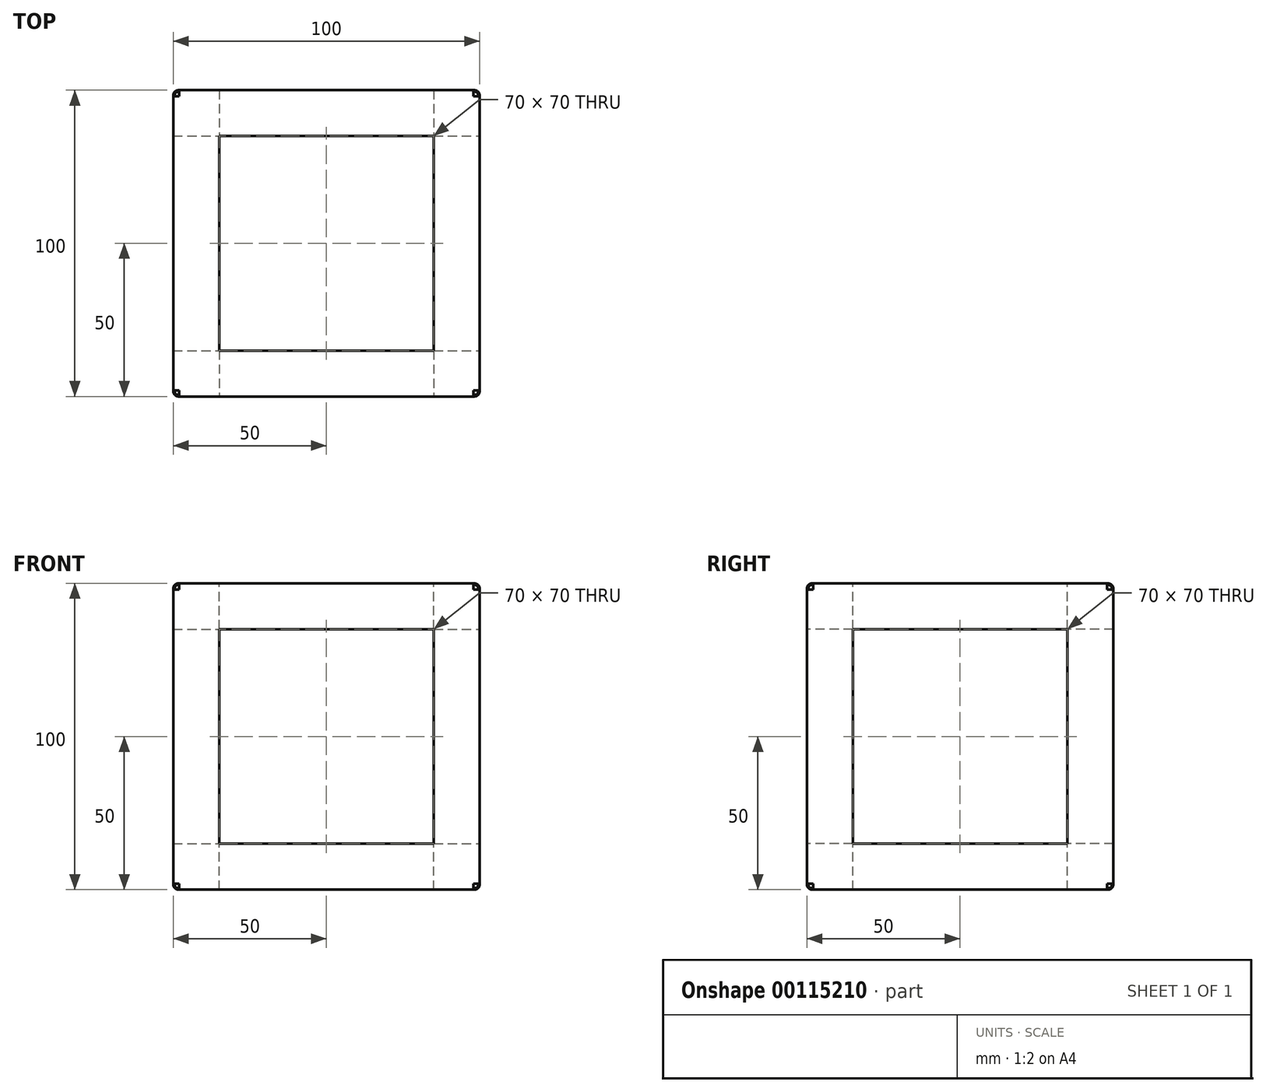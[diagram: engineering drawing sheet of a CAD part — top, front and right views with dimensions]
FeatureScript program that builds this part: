
annotation { "Feature Type Name" : "Feature", "Feature Type Description" : "" }
export const myFeature = defineFeature(function(context is Context, id is Id, definition is map)
    precondition{}
    {
        {
            var Q0;
            Q0=qCreatedBy(makeId("Front.planeOp"),FACE);
            var sketch = newSketch(context, id + "F0", { "sketchPlane" : qUnion([Q0])});
            skLineSegment(sketch, "E0.bottom", {"start": v(50, 50) * mm, "end": v(-50, 50) * mm});
            skLineSegment(sketch, "E0.top", {"start": v(50, -50) * mm, "end": v(-50, -50) * mm});
            skLineSegment(sketch, "E0.left", {"start": v(50, 50) * mm, "end": v(50, -50) * mm});
            skLineSegment(sketch, "E0.right", {"start": v(-50, 50) * mm, "end": v(-50, -50) * mm});
            skPoint(sketch, "E0.middle", {"position": v(0, 0) * mm});
            skSolve(sketch);
        }
        {
            var Q0;
            Q0 = qSketchRegion(id + "F0", true);
            var Q1;
            Q1=makeQuery(id+"F0.imprint","IMPRINT",FACE,{"disambiguationData":[TD([[makeQuery(id+"F0.imprint","IMPRINT",EDGE,{"derivedFrom":sQuery(id+"F0.wireOp",EDGE,"E0.bottom")}),1.0]])]});
            extrude(context, id + "F1", {"entities" : qUnion([Q0, Q1]), "endBound" : BoundingType.SYMMETRIC, "depth" : 100 * mm});
        }
        {
            var Q0;
            Q0=makeQuery(id+"F1.opExtrude","SWEPT_FACE",FACE,{"disambiguationData":[OSD([sQuery(id+"F0.wireOp",EDGE,"E0.bottom")])]});
            var sketch = newSketch(context, id + "F2", { "sketchPlane" : qUnion([Q0])});
            skLineSegment(sketch, "E1.0", {"start": v(35, 35) * mm, "end": v(-35, 35) * mm});
            skLineSegment(sketch, "E1.1", {"start": v(35, -35) * mm, "end": v(35, 35) * mm});
            skLineSegment(sketch, "E1.2", {"start": v(-35, -35) * mm, "end": v(35, -35) * mm});
            skLineSegment(sketch, "E1.3", {"start": v(-35, 35) * mm, "end": v(-35, -35) * mm});
            skSolve(sketch);
        }
        {
            var Q0;
            Q0 = qSketchRegion(id + "F2", true);
            extrude(context, id + "F3", {"entities" : qUnion([Q0]), "operationType" : NewBodyOperationType.REMOVE, "endBound" : BoundingType.THROUGH_ALL, "oppositeDirection" : true, "depth" : 25 * mm});
        }
        {
            var Q0;
            Q0=makeQuery(id+"F1.opExtrude","CAP_FACE",FACE,{"disambiguationData":[OSD([sQuery(id+"F0.wireOp",EDGE,"E0.bottom"),sQuery(id+"F0.wireOp",EDGE,"E0.top"),sQuery(id+"F0.wireOp",EDGE,"E0.left"),sQuery(id+"F0.wireOp",EDGE,"E0.right")])],"isStart":false});
            var sketch = newSketch(context, id + "F4", { "sketchPlane" : qUnion([Q0])});
            skLineSegment(sketch, "E2.0", {"start": v(35, -35) * mm, "end": v(35, 35) * mm});
            skLineSegment(sketch, "E2.1", {"start": v(-35, -35) * mm, "end": v(35, -35) * mm});
            skLineSegment(sketch, "E2.2", {"start": v(-35, 35) * mm, "end": v(-35, -35) * mm});
            skLineSegment(sketch, "E2.3", {"start": v(35, 35) * mm, "end": v(-35, 35) * mm});
            skSolve(sketch);
        }
        {
            var Q0;
            Q0 = qSketchRegion(id + "F4", true);
            extrude(context, id + "F5", {"entities" : qUnion([Q0]), "operationType" : NewBodyOperationType.REMOVE, "endBound" : BoundingType.THROUGH_ALL, "oppositeDirection" : true, "depth" : 25 * mm});
        }
        {
            var Q0;
            Q0=makeQuery(id+"F1.opExtrude","SWEPT_FACE",FACE,{"disambiguationData":[OSD([sQuery(id+"F0.wireOp",EDGE,"E0.left")])]});
            var sketch = newSketch(context, id + "F6", { "sketchPlane" : qUnion([Q0])});
            skLineSegment(sketch, "E3.0", {"start": v(35, -35) * mm, "end": v(35, 35) * mm});
            skLineSegment(sketch, "E3.1", {"start": v(-35, -35) * mm, "end": v(35, -35) * mm});
            skLineSegment(sketch, "E3.2", {"start": v(-35, 35) * mm, "end": v(-35, -35) * mm});
            skLineSegment(sketch, "E3.3", {"start": v(35, 35) * mm, "end": v(-35, 35) * mm});
            skSolve(sketch);
        }
        {
            var Q0;
            Q0 = qSketchRegion(id + "F6", true);
            extrude(context, id + "F7", {"entities" : qUnion([Q0]), "operationType" : NewBodyOperationType.REMOVE, "endBound" : BoundingType.THROUGH_ALL, "oppositeDirection" : true, "depth" : 25 * mm});
        }
        {
            var Q0;
            Q0=makeQuery(id+"F1.opExtrude","CAP_EDGE",EDGE,{"disambiguationData":[OSD([sQuery(id+"F0.wireOp",EDGE,"E0.bottom")])],"isStart":false});
            var Q1;
            Q1=makeQuery(id+"F1.opExtrude","SWEPT_EDGE",EDGE,{"disambiguationData":[OSD([sQuery(id+"F0.wireOp",EDGE,"E0.bottom"),sQuery(id+"F0.wireOp",EDGE,"E0.left")])]});
            var Q2;
            Q2=makeQuery(id+"F1.opExtrude","CAP_EDGE",EDGE,{"disambiguationData":[OSD([sQuery(id+"F0.wireOp",EDGE,"E0.bottom")])],"isStart":true});
            var Q3;
            Q3=makeQuery(id+"F1.opExtrude","SWEPT_EDGE",EDGE,{"disambiguationData":[OSD([sQuery(id+"F0.wireOp",EDGE,"E0.bottom"),sQuery(id+"F0.wireOp",EDGE,"E0.right")])]});
            var Q4;
            Q4=makeQuery(id+"F1.opExtrude","CAP_EDGE",EDGE,{"disambiguationData":[OSD([sQuery(id+"F0.wireOp",EDGE,"E0.top")])],"isStart":false});
            var Q5;
            Q5=makeQuery(id+"F1.opExtrude","SWEPT_EDGE",EDGE,{"disambiguationData":[OSD([sQuery(id+"F0.wireOp",EDGE,"E0.top"),sQuery(id+"F0.wireOp",EDGE,"E0.left")])]});
            var Q6;
            Q6=makeQuery(id+"F1.opExtrude","CAP_EDGE",EDGE,{"disambiguationData":[OSD([sQuery(id+"F0.wireOp",EDGE,"E0.top")])],"isStart":true});
            var Q7;
            Q7=makeQuery(id+"F1.opExtrude","SWEPT_EDGE",EDGE,{"disambiguationData":[OSD([sQuery(id+"F0.wireOp",EDGE,"E0.top"),sQuery(id+"F0.wireOp",EDGE,"E0.right")])]});
            var Q8;
            Q8=makeQuery(id+"F1.opExtrude","CAP_EDGE",EDGE,{"disambiguationData":[OSD([sQuery(id+"F0.wireOp",EDGE,"E0.left")])],"isStart":false});
            var Q9;
            Q9=makeQuery(id+"F1.opExtrude","CAP_EDGE",EDGE,{"disambiguationData":[OSD([sQuery(id+"F0.wireOp",EDGE,"E0.left")])],"isStart":true});
            var Q10;
            Q10=makeQuery(id+"F1.opExtrude","CAP_EDGE",EDGE,{"disambiguationData":[OSD([sQuery(id+"F0.wireOp",EDGE,"E0.right")])],"isStart":false});
            var Q11;
            Q11=makeQuery(id+"F1.opExtrude","CAP_EDGE",EDGE,{"disambiguationData":[OSD([sQuery(id+"F0.wireOp",EDGE,"E0.right")])],"isStart":true});
            fillet(context, id + "F8", {"entities" : qUnion([Q0, Q1, Q2, Q3, Q4, Q5, Q6, Q7, Q8, Q9, Q10, Q11]), "radius" : 2 * mm, "tangentPropagation" : true, "rho" : 0.5, "crossSection" : FilletCrossSection.CONIC, "allowEdgeOverflow" : false});
        }
    });
